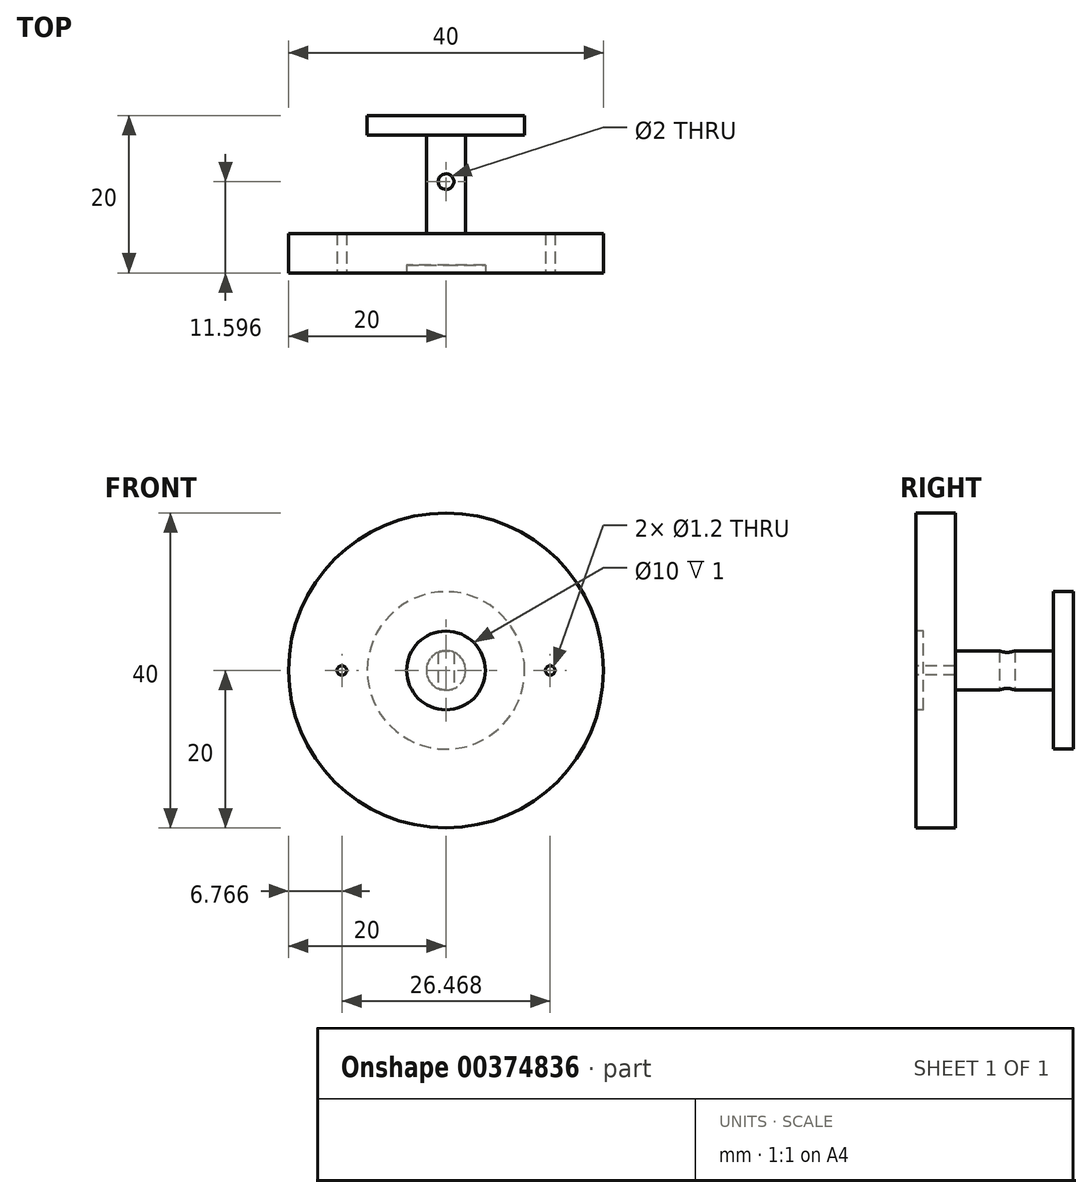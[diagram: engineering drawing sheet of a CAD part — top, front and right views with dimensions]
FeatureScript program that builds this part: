
annotation { "Feature Type Name" : "Feature", "Feature Type Description" : "" }
export const myFeature = defineFeature(function(context is Context, id is Id, definition is map)
    precondition{}
    {
        {
            var Q0;
            Q0=qCreatedBy(makeId("Front.planeOp"),FACE);
            var sketch = newSketch(context, id + "F0", { "sketchPlane" : qUnion([Q0])});
            skCircle(sketch, "E0", {"center": v(0, 0) * mm, "radius": 20 * mm});
            skLineSegment(sketch, "E1", {"start": v(-20, 0) * mm, "end": v(20, 0) * mm, "construction": true});
            skSolve(sketch);
        }
        {
            var Q0;
            Q0=makeQuery(id+"F0.imprint","IMPRINT",FACE,{"disambiguationData":[TD([[makeQuery(id+"F0.imprint","IMPRINT",EDGE,{"derivedFrom":sQuery(id+"F0.wireOp",EDGE,"E0")}),1.0]])]});
            var Q1;
            Q1=makeQuery(id+"F0.imprint","IMPRINT",FACE,{"disambiguationData":[TD([[makeQuery(id+"F0.imprint","IMPRINT",EDGE,{"derivedFrom":sQuery(id+"F0.wireOp",EDGE,"g4SzYNnp-7GX3-4Bz9-JgFw-h83czDQZXrlS")}),1.0]])]});
            var Q2;
            Q2=makeQuery(id+"F0.imprint","IMPRINT",FACE,{"disambiguationData":[TD([[makeQuery(id+"F0.imprint","IMPRINT",EDGE,{"derivedFrom":sQuery(id+"F0.wireOp",EDGE,"VTtGYPlZ-mSQm-bK6K-4VJF-H7FI5BS2IZTO")}),1.0]])]});
            extrude(context, id + "F1", {"entities" : qUnion([Q0, Q1, Q2]), "depth" : 5 * mm, "offsetDistance" : 25 * mm});
        }
        {
            var Q0;
            Q0=makeQuery(id+"F1.opExtrude","CAP_FACE",FACE,{"disambiguationData":[OSD([sQuery(id+"F0.wireOp",EDGE,"E0")])],"isStart":false});
            var sketch = newSketch(context, id + "F2", { "sketchPlane" : qUnion([Q0])});
            skLineSegment(sketch, "E2", {"start": v(-20, 0) * mm, "end": v(20, 0) * mm, "construction": true});
            skCircle(sketch, "E3", {"center": v(-13.23, 0) * mm, "radius": 0.6 * mm});
            skCircle(sketch, "E4", {"center": v(13.23, 0) * mm, "radius": 0.6 * mm});
            skPoint(sketch, "E5", {"position": v(0, 0) * mm});
            skSolve(sketch);
        }
        {
            var Q0;
            Q0=makeQuery(id+"F2.imprint","IMPRINT",FACE,{"disambiguationData":[TD([[makeQuery(id+"F2.imprint","IMPRINT",EDGE,{"derivedFrom":sQuery(id+"F2.wireOp",EDGE,"E3")}),1.0]])]});
            var Q1;
            Q1=makeQuery(id+"F2.imprint","IMPRINT",FACE,{"disambiguationData":[TD([[makeQuery(id+"F2.imprint","IMPRINT",EDGE,{"derivedFrom":sQuery(id+"F2.wireOp",EDGE,"E4")}),1.0]])]});
            var Q2;
            Q2=makeQuery(id+"F1.opExtrude","CAP_FACE",FACE,{"disambiguationData":[OSD([sQuery(id+"F0.wireOp",EDGE,"E0")])],"isStart":true});
            extrude(context, id + "F3", {"entities" : qUnion([Q0, Q1]), "operationType" : NewBodyOperationType.REMOVE, "endBound" : BoundingType.UP_TO_SURFACE, "oppositeDirection" : true, "depth" : 8.1 * mm, "endBoundEntityFace" : qUnion([Q2]), "offsetDistance" : 25 * mm});
        }
        {
            var Q0;
            Q0=makeQuery(id+"F0.imprint","IMPRINT",FACE,{"disambiguationData":[TD([[makeQuery(id+"F0.imprint","IMPRINT",EDGE,{"derivedFrom":sQuery(id+"F0.wireOp",EDGE,"E0")}),1.0]])]});
            var sketch = newSketch(context, id + "F4", { "sketchPlane" : qUnion([Q0])});
            skCircle(sketch, "E6", {"center": v(0, 0) * mm, "radius": 2.5 * mm});
            skSolve(sketch);
        }
        {
            var Q0;
            Q0=makeQuery(id+"F4.imprint","IMPRINT",FACE,{"disambiguationData":[TD([[makeQuery(id+"F4.imprint","IMPRINT",EDGE,{"derivedFrom":sQuery(id+"F4.wireOp",EDGE,"E6")}),1.0]])]});
            extrude(context, id + "F5", {"entities" : qUnion([Q0]), "operationType" : NewBodyOperationType.ADD, "oppositeDirection" : true, "depth" : 15 * mm, "offsetDistance" : 25 * mm});
        }
        {
            var Q0;
            Q0=qCreatedBy(makeId("Top.planeOp"),FACE);
            var sketch = newSketch(context, id + "F6", { "sketchPlane" : qUnion([Q0])});
            skLineSegment(sketch, "E7", {"start": v(0, -7.65) * mm, "end": v(0, 20.85) * mm, "construction": true});
            skCircle(sketch, "E8", {"center": v(0, 6.6) * mm, "radius": 1 * mm});
            skSolve(sketch);
        }
        {
            var Q0;
            Q0 = qSketchRegion(id + "F6", true);
            extrude(context, id + "F7", {"entities" : qUnion([Q0]), "operationType" : NewBodyOperationType.REMOVE, "depth" : 25 * mm, "offsetDistance" : 25 * mm, "hasSecondDirection" : true, "secondDirectionOppositeDirection" : true, "secondDirectionDepth" : 25 * mm});
        }
        {
            var Q0;
            Q0=makeQuery(id+"F2.imprint","IMPRINT",FACE,{"disambiguationData":[TD([[makeQuery(id+"F2.imprint","IMPRINT",EDGE,{"derivedFrom":sQuery(id+"F2.wireOp",EDGE,"E3")}),-1.0]])]});
            var sketch = newSketch(context, id + "F8", { "sketchPlane" : qUnion([Q0])});
            skCircle(sketch, "E9", {"center": v(0, 0) * mm, "radius": 5 * mm});
            skSolve(sketch);
        }
        {
            var Q0;
            Q0 = qSketchRegion(id + "F6", true);
            extrude(context, id + "F9", {"entities" : qUnion([Q0]), "operationType" : NewBodyOperationType.REMOVE, "oppositeDirection" : true, "depth" : 25 * mm, "offsetDistance" : 25 * mm, "hasSecondDirection" : true, "secondDirectionOppositeDirection" : false, "secondDirectionDepth" : 25 * mm});
        }
        {
            var Q0;
            Q0 = qSketchRegion(id + "F8", true);
            extrude(context, id + "F10", {"entities" : qUnion([Q0]), "operationType" : NewBodyOperationType.REMOVE, "oppositeDirection" : true, "depth" : 1 * mm, "offsetDistance" : 25 * mm});
        }
        {
            var Q0;
            Q0=makeQuery(id+"F5.opExtrude","CAP_FACE",FACE,{"disambiguationData":[OSD([sQuery(id+"F4.wireOp",EDGE,"E6")])],"isStart":false});
            var sketch = newSketch(context, id + "F11", { "sketchPlane" : qUnion([Q0])});
            skCircle(sketch, "E10", {"center": v(0, 0) * mm, "radius": 10 * mm});
            skSolve(sketch);
        }
        {
            var Q0;
            Q0 = qSketchRegion(id + "F11", true);
            extrude(context, id + "F12", {"entities" : qUnion([Q0]), "operationType" : NewBodyOperationType.ADD, "oppositeDirection" : true, "depth" : 2.5 * mm, "offsetDistance" : 25 * mm});
        }
    });
